# Revit family: 511_AWN_nailfin
name_source: partatom
category: Windows
revit_build: Autodesk Revit 2016 (Build: 20150220_1215(x64)
units: mm (PartAtom-declared; Revit-internal decimal feet)

## family parameters
Always vertical = Yes
Cut with Voids When Loaded = No
Host = Wall
OmniClass Number = 23.30.20.00
OmniClass Title = Windows
Room Calculation Point = No
Shared = No

## types (17) — shared parameters
Default Sill Height = 31 1/2"
MH = 3 1/4"
Wall Closure = By host

## per-type parameters (varying)
| type | Height | MW | Width |
| 24x30 | 30" | 12" | 24" |
| 48x32Max | 32" | 24" | 48" |
| 15x12Min | 12" | 7 1/2" | 15" |
| 36x32 | 32" | 18" | 36" |
| 15x18 | 18" | 7 1/2" | 15" |
| 15x24 | 24" | 7 1/2" | 15" |
| 18x24 | 24" | 9" | 18" |
| 18x18 | 18" | 9" | 18" |
| 18x30 | 30" | 9" | 18" |
| 24x18 | 18" | 12" | 24" |
| 18x12 | 12" | 9" | 18" |
| 24x12 | 12" | 12" | 24" |
| 36x12 | 12" | 18" | 36" |
| 36x18 | 18" | 18" | 36" |
| 36x24 | 24" | 18" | 36" |
| 48x18 | 18" | 24" | 48" |
| 48x24 | 24" | 24" | 48" |

## geometry (parser evidence)
native form markers: Sweep x1
no freeform markers — native parametric forms only
